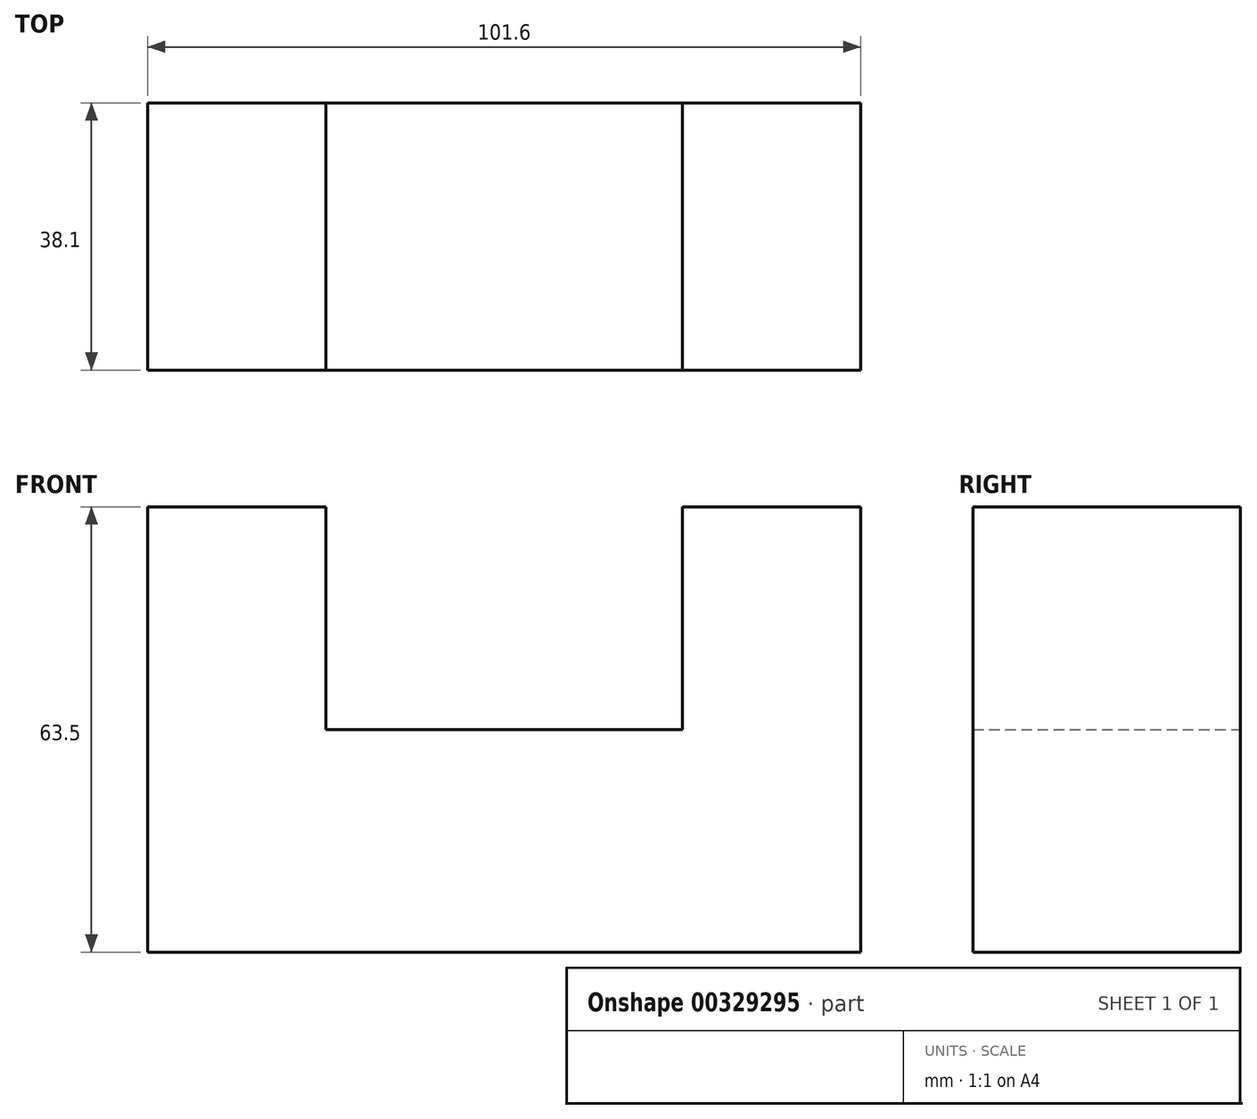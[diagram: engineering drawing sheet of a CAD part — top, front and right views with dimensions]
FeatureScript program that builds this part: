
annotation { "Feature Type Name" : "Feature", "Feature Type Description" : "" }
export const myFeature = defineFeature(function(context is Context, id is Id, definition is map)
    precondition{}
    {
        {
            var Q0;
            Q0=qCreatedBy(makeId("Front.planeOp"),FACE);
            var sketch = newSketch(context, id + "F0", { "sketchPlane" : qUnion([Q0])});
            skLineSegment(sketch, "E0", {"start": v(-52.3, -28.42) * mm, "end": v(49.3, -28.42) * mm});
            skLineSegment(sketch, "E1", {"start": v(49.3, -28.42) * mm, "end": v(49.3, 35.08) * mm});
            skLineSegment(sketch, "E2", {"start": v(49.3, 35.08) * mm, "end": v(23.9, 35.08) * mm});
            skLineSegment(sketch, "E3", {"start": v(23.9, 35.08) * mm, "end": v(23.9, 3.33) * mm});
            skLineSegment(sketch, "E4", {"start": v(23.9, 3.33) * mm, "end": v(-26.9, 3.33) * mm});
            skLineSegment(sketch, "E5", {"start": v(-26.9, 3.33) * mm, "end": v(-26.9, 35.08) * mm});
            skLineSegment(sketch, "E6", {"start": v(-26.9, 35.08) * mm, "end": v(-52.3, 35.08) * mm});
            skLineSegment(sketch, "E7", {"start": v(-52.3, 35.08) * mm, "end": v(-52.3, -28.42) * mm});
            skSolve(sketch);
        }
        {
            var Q0;
            Q0 = qSketchRegion(id + "F0", true);
            extrude(context, id + "F1", {"entities" : qUnion([Q0]), "depth" : 38.1 * mm});
        }
    });
